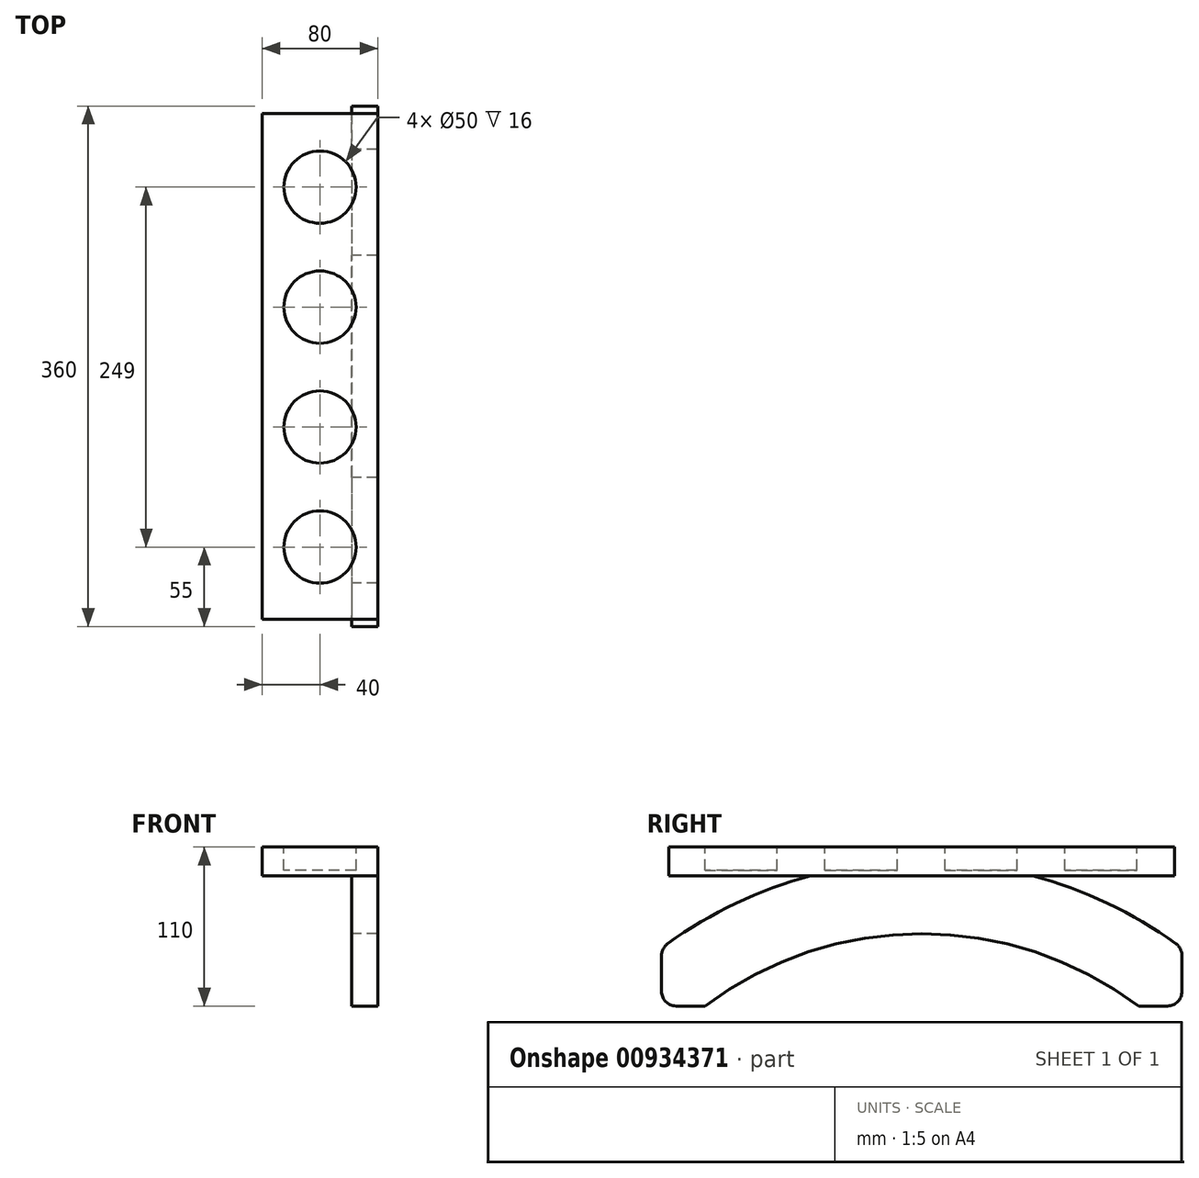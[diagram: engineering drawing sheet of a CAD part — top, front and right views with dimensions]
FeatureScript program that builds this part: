
annotation { "Feature Type Name" : "Feature", "Feature Type Description" : "" }
export const myFeature = defineFeature(function(context is Context, id is Id, definition is map)
    precondition{}
    {
        {
            var Q0;
            Q0=qCreatedBy(makeId("Right.planeOp"),FACE);
            var sketch = newSketch(context, id + "F0", { "sketchPlane" : qUnion([Q0])});
            skArc(sketch, "E0", {"start": v(150, 0) * mm, "mid": v(0, 50) * mm, "end": v(-150, 0) * mm});
            skArc(sketch, "E1.0", {"start": v(175.86, 43.05) * mm, "mid": v(128.5, 71.09) * mm, "end": v(76.81, 90) * mm});
            skLineSegment(sketch, "E2", {"start": v(-150, 0) * mm, "end": v(-170, 0) * mm});
            skLineSegment(sketch, "E3", {"start": v(150, 0) * mm, "end": v(170, 0) * mm});
            skLineSegment(sketch, "E4", {"start": v(-180, 34.95) * mm, "end": v(-180, 10) * mm});
            skLineSegment(sketch, "E5", {"start": v(180, 34.95) * mm, "end": v(180, 10) * mm});
            skLineSegment(sketch, "E6", {"start": v(-76.81, 90) * mm, "end": v(76.81, 90) * mm});
            skArc(sketch, "E7.trimOffspring", {"start": v(-76.81, 90) * mm, "mid": v(-128.5, 71.09) * mm, "end": v(-175.86, 43.05) * mm});
            skPoint(sketch, "E8.visualSharp", {"position": v(-180, 40) * mm});
            skArc(sketch, "E8.filletArc", {"start": v(-175.86, 43.05) * mm, "mid": v(-178.9, 39.5) * mm, "end": v(-180, 34.95) * mm});
            skPoint(sketch, "E9.visualSharp", {"position": v(180, 40) * mm});
            skArc(sketch, "E9.filletArc", {"start": v(180, 34.95) * mm, "mid": v(178.9, 39.5) * mm, "end": v(175.86, 43.05) * mm});
            skPoint(sketch, "E10.visualSharp", {"position": v(180, 0) * mm});
            skArc(sketch, "E10.filletArc", {"start": v(170, 0) * mm, "mid": v(177.07, 2.93) * mm, "end": v(180, 10) * mm});
            skPoint(sketch, "E11.visualSharp", {"position": v(-180, 0) * mm});
            skArc(sketch, "E11.filletArc", {"start": v(-180, 10) * mm, "mid": v(-177.07, 2.93) * mm, "end": v(-170, 0) * mm});
            skSolve(sketch);
        }
        {
            var Q0;
            Q0=makeQuery(id+"F0.imprint","IMPRINT",FACE,{"disambiguationData":[TD([[makeQuery(id+"F0.imprint","IMPRINT",EDGE,{"derivedFrom":sQuery(id+"F0.wireOp",EDGE,"E0")}),-1.0]])]});
            extrude(context, id + "F1", {"entities" : qUnion([Q0]), "depth" : 18 * mm, "offsetDistance" : 25 * mm});
        }
        {
            var Q0;
            Q0=makeQuery(id+"F1.opExtrude","SWEPT_FACE",FACE,{"disambiguationData":[OSD([sQuery(id+"F0.wireOp",EDGE,"E6")])]});
            var sketch = newSketch(context, id + "F2", { "sketchPlane" : qUnion([Q0])});
            skLineSegment(sketch, "E12.bottom", {"start": v(18, -175) * mm, "end": v(-62, -175) * mm});
            skLineSegment(sketch, "E12.top", {"start": v(18, 175) * mm, "end": v(-62, 175) * mm});
            skLineSegment(sketch, "E12.left", {"start": v(18, -175) * mm, "end": v(18, 175) * mm});
            skLineSegment(sketch, "E12.right", {"start": v(-62, -175) * mm, "end": v(-62, 175) * mm});
            skLineSegment(sketch, "E13", {"start": v(0, 0) * mm, "end": v(-148.8, 0) * mm, "construction": true});
            skSolve(sketch);
        }
        {
            var Q0;
            Q0 = qSketchRegion(id + "F2", true);
            extrude(context, id + "F3", {"entities" : qUnion([Q0]), "depth" : 20 * mm, "offsetDistance" : 25 * mm});
        }
        {
            var Q0;
            Q0=makeQuery(id+"F3.opExtrude","CAP_FACE",FACE,{"disambiguationData":[OSD([sQuery(id+"F2.wireOp",EDGE,"E12.bottom"),sQuery(id+"F2.wireOp",EDGE,"E12.top"),sQuery(id+"F2.wireOp",EDGE,"E12.left"),sQuery(id+"F2.wireOp",EDGE,"E12.right")])],"isStart":false});
            var sketch = newSketch(context, id + "F4", { "sketchPlane" : qUnion([Q0])});
            skCircle(sketch, "E14", {"center": v(-22, -125) * mm, "radius": 25 * mm});
            skPoint(sketch, "E14.centerSnap0", {"position": v(-22, -175) * mm});
            skCircle(sketch, "E15.0.1.0", {"center": v(-22, -42) * mm, "radius": 25 * mm});
            skCircle(sketch, "E15.0.2.0", {"center": v(-22, 41) * mm, "radius": 25 * mm});
            skCircle(sketch, "E15.0.3.0", {"center": v(-22, 124) * mm, "radius": 25 * mm});
            skLineSegment(sketch, "E15.direction1", {"start": v(-22, -125) * mm, "end": v(3, -125) * mm, "construction": true});
            skLineSegment(sketch, "E15.direction2", {"start": v(-22, -125) * mm, "end": v(-22, -42) * mm, "construction": true});
            skSolve(sketch);
        }
        {
            var Q0;
            Q0 = qSketchRegion(id + "F4", true);
            extrude(context, id + "F5", {"entities" : qUnion([Q0]), "operationType" : NewBodyOperationType.REMOVE, "oppositeDirection" : true, "depth" : 16 * mm, "offsetDistance" : 25 * mm});
        }
    });
